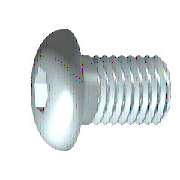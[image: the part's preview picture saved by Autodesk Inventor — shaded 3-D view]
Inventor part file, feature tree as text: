
AUTODESK INVENTOR PART (.ipt)
format: ipt  version: 2024.2 (Build 282272000, 272)  size: 214,528 bytes
history: native  units: mm (DEFAULTED — no unit token found)
features: extrude x1, plane x1, fillet x1
ambient origin geometry x7: Origin, YZ Plane, XY Plane, X Axis, Y Axis, Z Axis, Center Point
bodies: Solid1 (feature_tree), Body (feature_tree)
feature tree (3):
  extrude  "Slot"  Depth=4.5mm
  plane  "Work Plane1"
  fillet  "Fillet2"  Radius=0.306825mm
